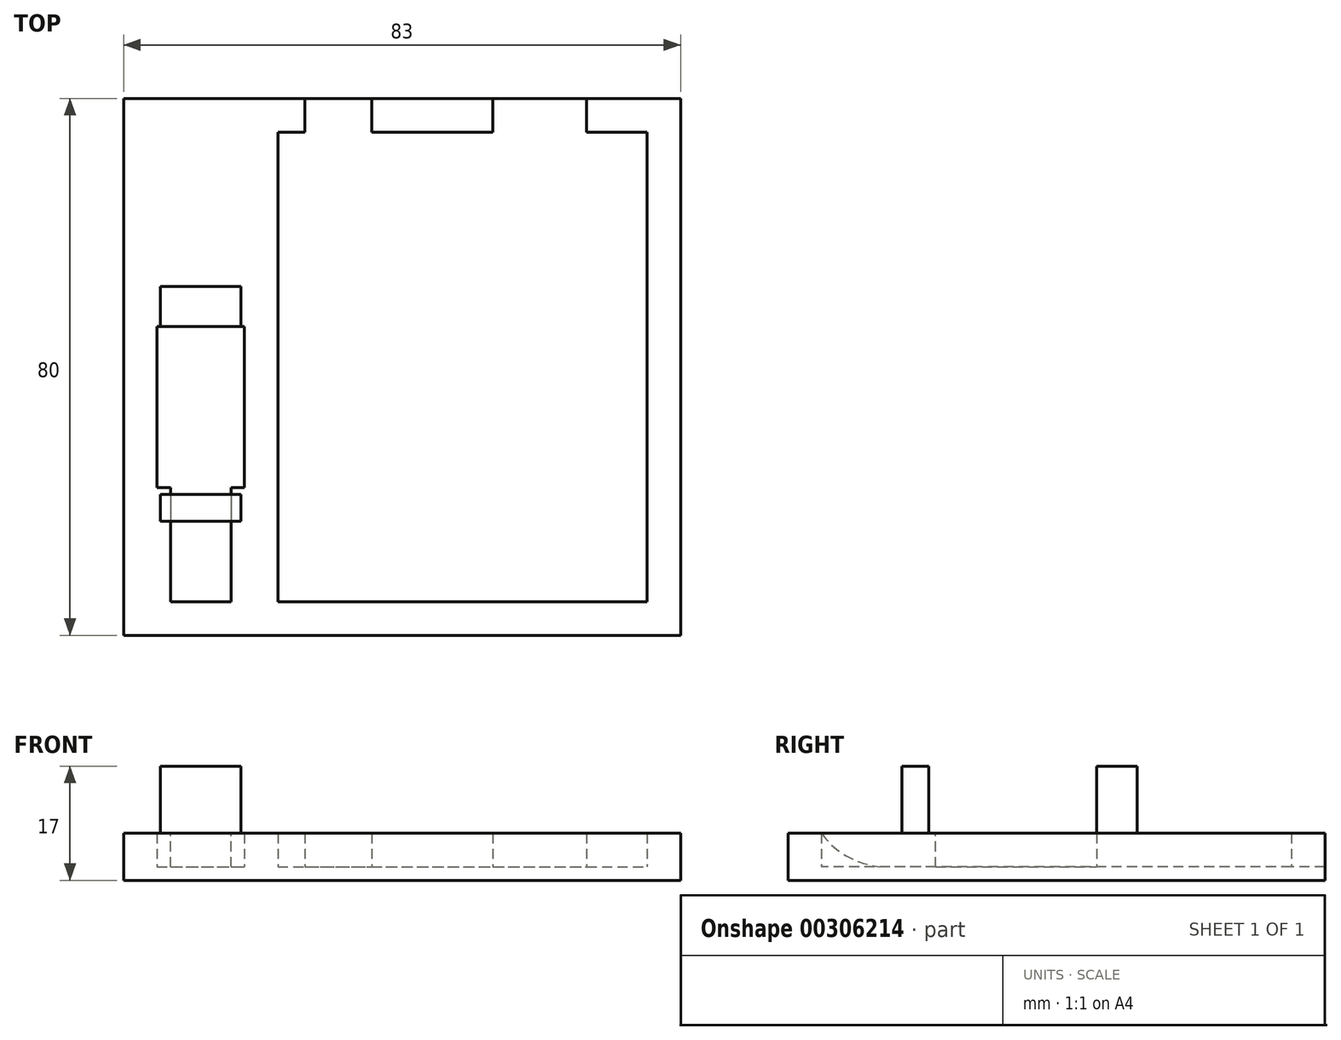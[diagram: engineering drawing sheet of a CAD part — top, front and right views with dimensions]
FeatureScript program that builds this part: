
annotation { "Feature Type Name" : "Feature", "Feature Type Description" : "" }
export const myFeature = defineFeature(function(context is Context, id is Id, definition is map)
    precondition{}
    {
        {
            var Q0;
            Q0=qCreatedBy(makeId("Top.planeOp"),FACE);
            var sketch = newSketch(context, id + "F0", { "sketchPlane" : qUnion([Q0])});
            skLineSegment(sketch, "E0.bottom", {"start": v(-46.71, 42.48) * mm, "end": v(36.29, 42.48) * mm});
            skLineSegment(sketch, "E0.top", {"start": v(-46.71, -37.52) * mm, "end": v(36.29, -37.52) * mm});
            skLineSegment(sketch, "E0.left", {"start": v(-46.71, 42.48) * mm, "end": v(-46.71, -37.52) * mm});
            skLineSegment(sketch, "E0.right", {"start": v(36.29, 42.48) * mm, "end": v(36.29, -37.52) * mm});
            skLineSegment(sketch, "E1.bottom", {"start": v(22.29, 42.48) * mm, "end": v(8.29, 42.48) * mm});
            skLineSegment(sketch, "E1.top", {"start": v(22.29, 37.48) * mm, "end": v(8.29, 37.48) * mm});
            skLineSegment(sketch, "E1.left", {"start": v(22.29, 42.48) * mm, "end": v(22.29, 37.48) * mm});
            skLineSegment(sketch, "E1.right", {"start": v(8.29, 42.48) * mm, "end": v(8.29, 37.48) * mm});
            skLineSegment(sketch, "E2.bottom", {"start": v(-19.71, 42.48) * mm, "end": v(-9.71, 42.48) * mm});
            skLineSegment(sketch, "E2.top", {"start": v(-19.71, 37.48) * mm, "end": v(-9.71, 37.48) * mm});
            skLineSegment(sketch, "E2.left", {"start": v(-19.71, 42.48) * mm, "end": v(-19.71, 37.48) * mm});
            skLineSegment(sketch, "E2.right", {"start": v(-9.71, 42.48) * mm, "end": v(-9.71, 37.48) * mm});
            skLineSegment(sketch, "E3.bottom", {"start": v(-23.71, 37.48) * mm, "end": v(31.29, 37.48) * mm});
            skLineSegment(sketch, "E3.top", {"start": v(-23.71, -32.52) * mm, "end": v(31.29, -32.52) * mm});
            skLineSegment(sketch, "E3.left", {"start": v(-23.71, 37.48) * mm, "end": v(-23.71, -32.52) * mm});
            skLineSegment(sketch, "E3.right", {"start": v(31.29, 37.48) * mm, "end": v(31.29, -32.52) * mm});
            skLineSegment(sketch, "E4.bottom", {"start": v(-41.71, -15.52) * mm, "end": v(-28.71, -15.52) * mm});
            skLineSegment(sketch, "E4.top", {"start": v(-41.71, 8.48) * mm, "end": v(-28.71, 8.48) * mm});
            skLineSegment(sketch, "E4.left", {"start": v(-41.71, -15.52) * mm, "end": v(-41.71, 8.48) * mm});
            skLineSegment(sketch, "E4.right", {"start": v(-28.71, -15.52) * mm, "end": v(-28.71, 8.48) * mm});
            skSolve(sketch);
        }
        {
            var Q0;
            Q0=makeQuery(id+"F0.imprint","IMPRINT",FACE,{"disambiguationData":[TD([[makeQuery(id+"F0.imprint","IMPRINT",EDGE,{"derivedFrom":sQuery(id+"F0.wireOp",EDGE,"E0.top")}),1.0]])]});
            var Q1;
            {var subQ0=sQuery(id+"F0.wireOp",EDGE,"E1.right");Q1=makeQuery(id+"F0.imprint","IMPRINT",FACE,{"disambiguationData":[TD([[makeQuery(id+"F0.imprint","IMPRINT",EDGE,{"derivedFrom":subQ0}),-1.0]])]});}
            extrude(context, id + "F1", {"entities" : qUnion([Q0, Q1]), "depth" : 5 * mm});
        }
        {
            var Q0;
            Q0=makeQuery(id+"F1.opExtrude","CAP_FACE",FACE,{"disambiguationData":[OSD([sQuery(id+"F0.wireOp",EDGE,"E0.bottom"),sQuery(id+"F0.wireOp",EDGE,"E0.top"),sQuery(id+"F0.wireOp",EDGE,"E0.left"),sQuery(id+"F0.wireOp",EDGE,"E0.right"),sQuery(id+"F0.wireOp",EDGE,"E1.left"),sQuery(id+"F0.wireOp",EDGE,"E2.left"),sQuery(id+"F0.wireOp",EDGE,"E3.bottom"),sQuery(id+"F0.wireOp",EDGE,"E3.top"),sQuery(id+"F0.wireOp",EDGE,"E3.left"),sQuery(id+"F0.wireOp",EDGE,"E3.right"),sQuery(id+"F0.wireOp",EDGE,"E4.bottom"),sQuery(id+"F0.wireOp",EDGE,"E4.top"),sQuery(id+"F0.wireOp",EDGE,"E4.left"),sQuery(id+"F0.wireOp",EDGE,"E4.right")])],"isStart":true});
            var sketch = newSketch(context, id + "F2", { "sketchPlane" : qUnion([Q0])});
            skLineSegment(sketch, "E5.bottom", {"start": v(-46.71, 37.52) * mm, "end": v(36.29, 37.52) * mm});
            skLineSegment(sketch, "E5.top", {"start": v(-46.71, -42.48) * mm, "end": v(36.29, -42.48) * mm});
            skLineSegment(sketch, "E5.left", {"start": v(-46.71, 37.52) * mm, "end": v(-46.71, -42.48) * mm});
            skLineSegment(sketch, "E5.right", {"start": v(36.29, 37.52) * mm, "end": v(36.29, -42.48) * mm});
            skSolve(sketch);
        }
        {
            var Q0;
            Q0 = qSketchRegion(id + "F2", true);
            extrude(context, id + "F3", {"entities" : qUnion([Q0]), "operationType" : NewBodyOperationType.ADD, "depth" : 2 * mm});
        }
        {
            var Q0;
            Q0=makeQuery(id+"F1.opExtrude","CAP_FACE",FACE,{"disambiguationData":[OSD([sQuery(id+"F0.wireOp",EDGE,"E0.bottom"),sQuery(id+"F0.wireOp",EDGE,"E0.top"),sQuery(id+"F0.wireOp",EDGE,"E0.left"),sQuery(id+"F0.wireOp",EDGE,"E0.right"),sQuery(id+"F0.wireOp",EDGE,"E1.left"),sQuery(id+"F0.wireOp",EDGE,"E2.left"),sQuery(id+"F0.wireOp",EDGE,"E3.bottom"),sQuery(id+"F0.wireOp",EDGE,"E3.top"),sQuery(id+"F0.wireOp",EDGE,"E3.left"),sQuery(id+"F0.wireOp",EDGE,"E3.right"),sQuery(id+"F0.wireOp",EDGE,"E4.bottom"),sQuery(id+"F0.wireOp",EDGE,"E4.top"),sQuery(id+"F0.wireOp",EDGE,"E4.left"),sQuery(id+"F0.wireOp",EDGE,"E4.right")])],"isStart":false});
            var sketch = newSketch(context, id + "F4", { "sketchPlane" : qUnion([Q0])});
            skLineSegment(sketch, "E6.bottom", {"start": v(-30.71, -15.52) * mm, "end": v(-39.71, -15.52) * mm});
            skLineSegment(sketch, "E6.top", {"start": v(-30.71, -32.52) * mm, "end": v(-39.71, -32.52) * mm});
            skLineSegment(sketch, "E6.left", {"start": v(-30.71, -15.52) * mm, "end": v(-30.71, -32.52) * mm});
            skLineSegment(sketch, "E6.right", {"start": v(-39.71, -15.52) * mm, "end": v(-39.71, -32.52) * mm});
            skLineSegment(sketch, "E7", {"start": v(-35.21, -32.52) * mm, "end": v(-35.21, -15.52) * mm, "construction": true});
            skSolve(sketch);
        }
        {
            var Q0;
            Q0 = qSketchRegion(id + "F4", true);
            extrude(context, id + "F5", {"entities" : qUnion([Q0]), "operationType" : NewBodyOperationType.REMOVE, "oppositeDirection" : true, "depth" : 5 * mm});
        }
        {
            var Q0;
            Q0=makeQuery(id+"F1.opExtrude","CAP_FACE",FACE,{"disambiguationData":[OSD([sQuery(id+"F0.wireOp",EDGE,"E0.bottom"),sQuery(id+"F0.wireOp",EDGE,"E0.top"),sQuery(id+"F0.wireOp",EDGE,"E0.left"),sQuery(id+"F0.wireOp",EDGE,"E0.right"),sQuery(id+"F0.wireOp",EDGE,"E1.left"),sQuery(id+"F0.wireOp",EDGE,"E2.left"),sQuery(id+"F0.wireOp",EDGE,"E3.bottom"),sQuery(id+"F0.wireOp",EDGE,"E3.top"),sQuery(id+"F0.wireOp",EDGE,"E3.left"),sQuery(id+"F0.wireOp",EDGE,"E3.right"),sQuery(id+"F0.wireOp",EDGE,"E4.bottom"),sQuery(id+"F0.wireOp",EDGE,"E4.top"),sQuery(id+"F0.wireOp",EDGE,"E4.left"),sQuery(id+"F0.wireOp",EDGE,"E4.right")])],"isStart":false});
            var sketch = newSketch(context, id + "F6", { "sketchPlane" : qUnion([Q0])});
            skLineSegment(sketch, "E8.bottom", {"start": v(-29.21, 8.48) * mm, "end": v(-41.21, 8.48) * mm});
            skLineSegment(sketch, "E8.top", {"start": v(-29.21, 14.48) * mm, "end": v(-41.21, 14.48) * mm});
            skLineSegment(sketch, "E8.left", {"start": v(-29.21, 8.48) * mm, "end": v(-29.21, 14.48) * mm});
            skLineSegment(sketch, "E8.right", {"start": v(-41.21, 8.48) * mm, "end": v(-41.21, 14.48) * mm});
            skPoint(sketch, "E9", {"position": v(-35.21, 8.48) * mm});
            skSolve(sketch);
        }
        {
            var Q0;
            Q0 = qSketchRegion(id + "F6", true);
            extrude(context, id + "F7", {"entities" : qUnion([Q0]), "operationType" : NewBodyOperationType.ADD, "depth" : 10 * mm});
        }
        {
            var Q0;
            Q0=makeQuery(id+"F1.opExtrude","CAP_FACE",FACE,{"disambiguationData":[OSD([sQuery(id+"F0.wireOp",EDGE,"E0.bottom"),sQuery(id+"F0.wireOp",EDGE,"E0.top"),sQuery(id+"F0.wireOp",EDGE,"E0.left"),sQuery(id+"F0.wireOp",EDGE,"E0.right"),sQuery(id+"F0.wireOp",EDGE,"E1.left"),sQuery(id+"F0.wireOp",EDGE,"E2.left"),sQuery(id+"F0.wireOp",EDGE,"E3.bottom"),sQuery(id+"F0.wireOp",EDGE,"E3.top"),sQuery(id+"F0.wireOp",EDGE,"E3.left"),sQuery(id+"F0.wireOp",EDGE,"E3.right"),sQuery(id+"F0.wireOp",EDGE,"E4.bottom"),sQuery(id+"F0.wireOp",EDGE,"E4.top"),sQuery(id+"F0.wireOp",EDGE,"E4.left"),sQuery(id+"F0.wireOp",EDGE,"E4.right")])],"isStart":false});
            var sketch = newSketch(context, id + "F8", { "sketchPlane" : qUnion([Q0])});
            skLineSegment(sketch, "E10.bottom", {"start": v(-41.21, -16.52) * mm, "end": v(-29.21, -16.52) * mm});
            skLineSegment(sketch, "E10.top", {"start": v(-41.21, -20.52) * mm, "end": v(-29.21, -20.52) * mm});
            skLineSegment(sketch, "E10.left", {"start": v(-41.21, -16.52) * mm, "end": v(-41.21, -20.52) * mm});
            skLineSegment(sketch, "E10.right", {"start": v(-29.21, -16.52) * mm, "end": v(-29.21, -20.52) * mm});
            skSolve(sketch);
        }
        {
            var Q0;
            Q0 = qSketchRegion(id + "F8", true);
            extrude(context, id + "F9", {"entities" : qUnion([Q0]), "operationType" : NewBodyOperationType.ADD, "depth" : 10 * mm});
        }
        {
            var Q0;
            Q0=makeQuery(id+"F5.boolean.opBoolean","COPY",EDGE,{"derivedFrom":makeQuery(id+"F5.opExtrude","CAP_EDGE",EDGE,{"disambiguationData":[OSD([sQuery(id+"F4.wireOp",EDGE,"E6.top")])],"isStart":false})});
            fillet(context, id + "F10", {"entities" : qUnion([Q0]), "radius" : 12 * mm, "tangentPropagation" : true, "allowEdgeOverflow" : false});
        }
    });
